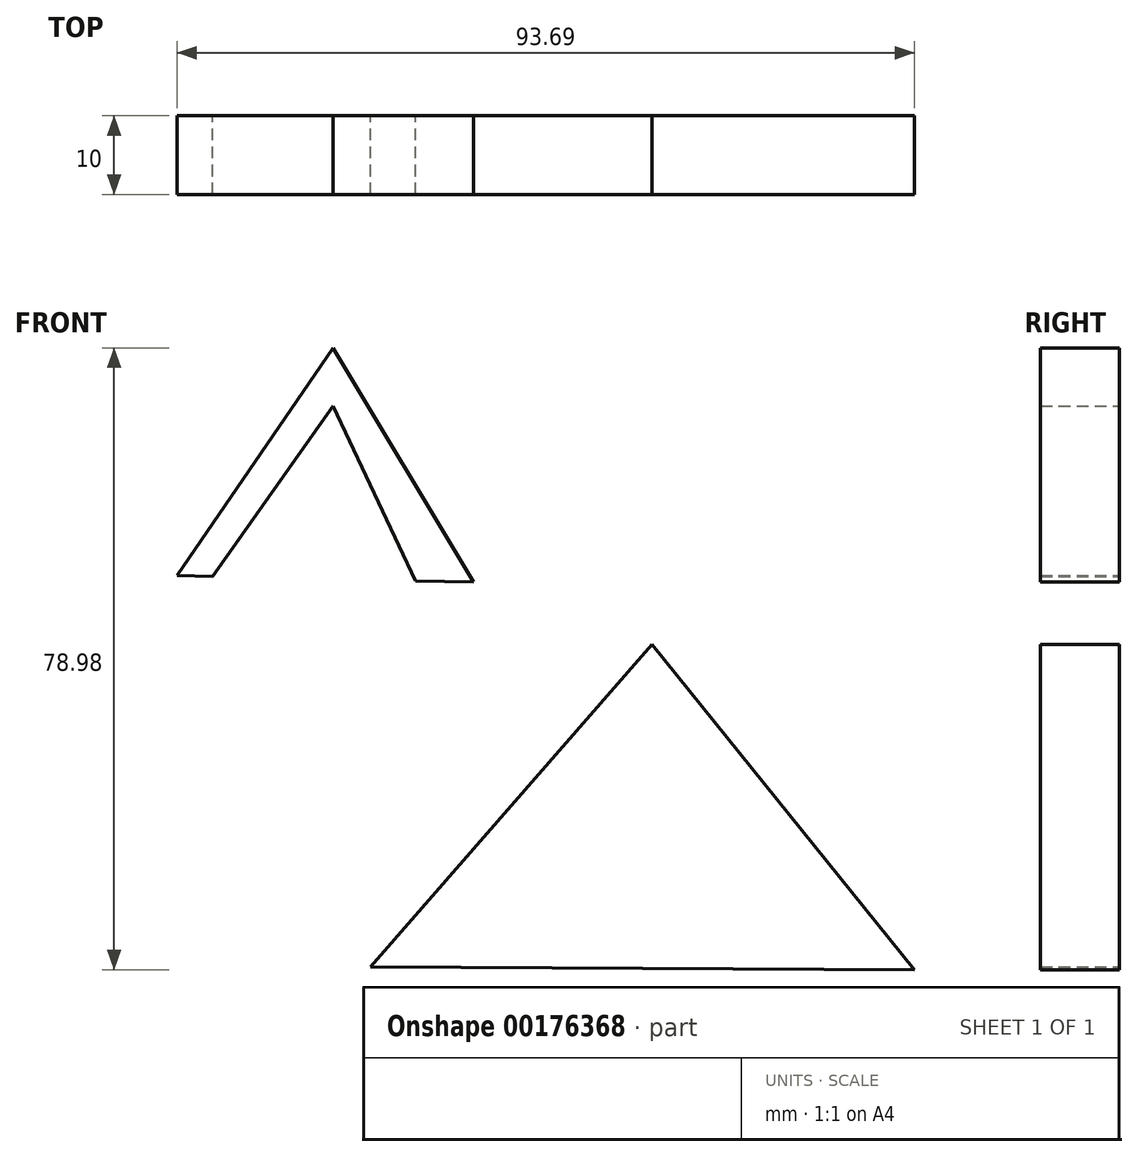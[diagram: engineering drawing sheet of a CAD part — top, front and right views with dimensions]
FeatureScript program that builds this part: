
annotation { "Feature Type Name" : "Feature", "Feature Type Description" : "" }
export const myFeature = defineFeature(function(context is Context, id is Id, definition is map)
    precondition{}
    {
        {
            var Q0;
            Q0=qCreatedBy(makeId("Front.planeOp"),FACE);
            var sketch = newSketch(context, id + "F0", { "sketchPlane" : qUnion([Q0])});
            skFitSpline(sketch, "E0", {"points": [v(-3.74, 41.73) * mm, v(-37.41, -23.6) * mm, v(10.94, -19.28) * mm], "startDerivative": vector(-107.62, -153.75) * mm, "endDerivative": vector(145.7, 38.34) * mm});
            skSolve(sketch);
        }
        {
            var Q0;
            Q0=qCreatedBy(makeId("Front.planeOp"),FACE);
            var sketch = newSketch(context, id + "F1", { "sketchPlane" : qUnion([Q0])});
            skLineSegment(sketch, "E1", {"start": v(-35.78, -40.96) * mm, "end": v(0, 0) * mm});
            skLineSegment(sketch, "E2", {"start": v(0, 0) * mm, "end": v(33.35, -41.3) * mm});
            skLineSegment(sketch, "E3", {"start": v(-35.78, -40.96) * mm, "end": v(33.35, -41.3) * mm});
            skSolve(sketch);
        }
        {
            var Q0;
            Q0 = qSketchRegion(id + "F1", true);
            extrude(context, id + "F2", {"entities" : qUnion([Q0]), "depth" : 10 * mm});
        }
        {
            var Q0;
            Q0=qCreatedBy(makeId("Front.planeOp"),FACE);
            var sketch = newSketch(context, id + "F3", { "sketchPlane" : qUnion([Q0])});
            skLineSegment(sketch, "E4", {"start": v(-60.34, 8.78) * mm, "end": v(-40.5, 37.68) * mm});
            skLineSegment(sketch, "E5", {"start": v(-40.5, 37.68) * mm, "end": v(-22.66, 7.93) * mm});
            skLineSegment(sketch, "E6", {"start": v(-60.34, 8.78) * mm, "end": v(-55.8, 8.68) * mm});
            skLineSegment(sketch, "E7", {"start": v(-30.02, 8.1) * mm, "end": v(-40.5, 30.31) * mm});
            skLineSegment(sketch, "E8", {"start": v(-40.5, 30.31) * mm, "end": v(-55.8, 8.68) * mm});
            skLineSegment(sketch, "E9.trimOffspring", {"start": v(-30.02, 8.1) * mm, "end": v(-22.66, 7.93) * mm});
            skSolve(sketch);
        }
        {
            var Q0;
            Q0=makeQuery(id+"F3.imprint","IMPRINT",FACE,{"disambiguationData":[TD([[makeQuery(id+"F3.imprint","IMPRINT",EDGE,{"derivedFrom":sQuery(id+"F3.wireOp",EDGE,"E4")}),-1.0]])]});
            extrude(context, id + "F4", {"entities" : qUnion([Q0]), "depth" : 10 * mm});
        }
    });
